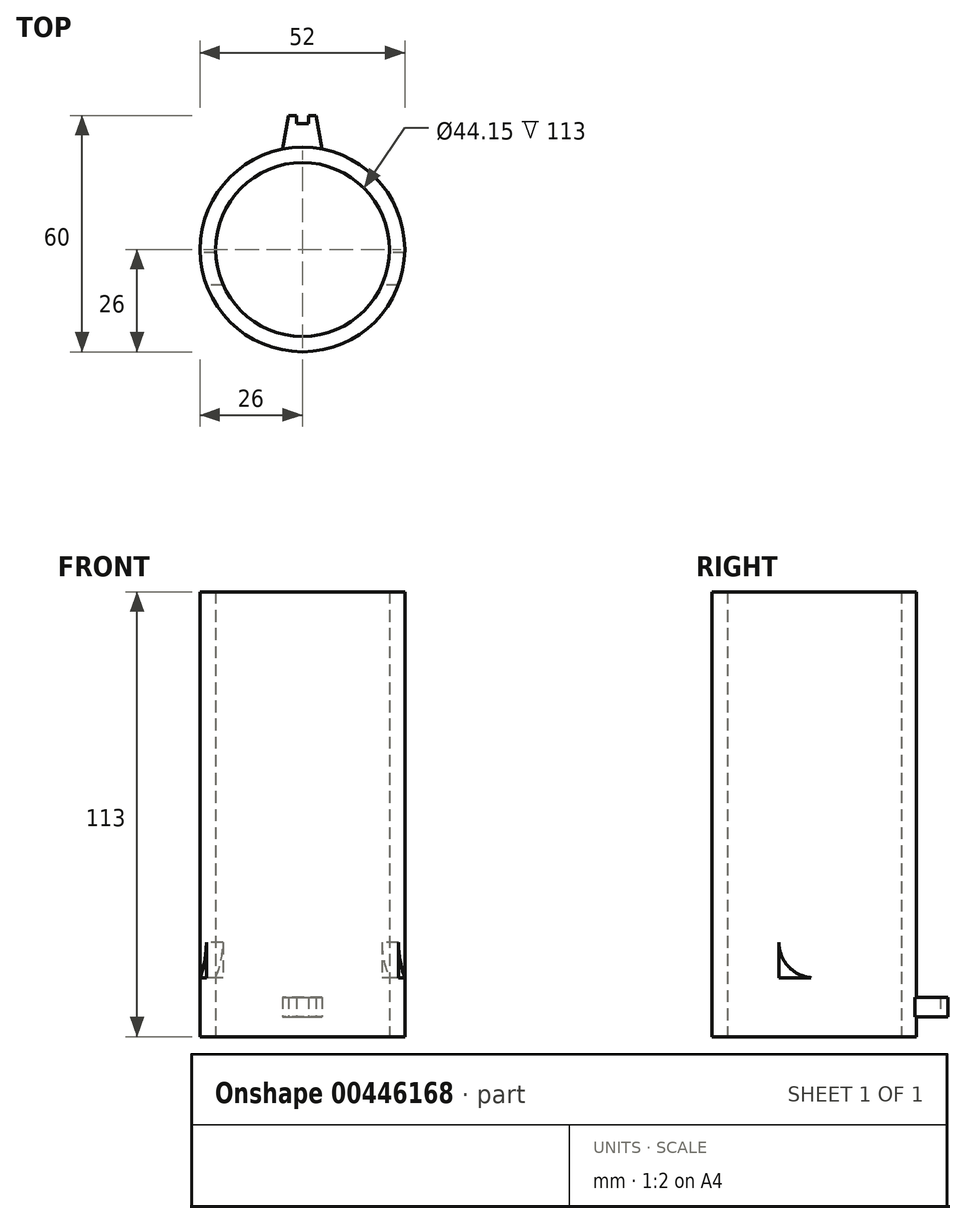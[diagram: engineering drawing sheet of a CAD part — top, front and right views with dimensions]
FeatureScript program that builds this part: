
annotation { "Feature Type Name" : "Feature", "Feature Type Description" : "" }
export const myFeature = defineFeature(function(context is Context, id is Id, definition is map)
    precondition{}
    {
        {
            var Q0;
            Q0=qCreatedBy(makeId("Top.planeOp"),FACE);
            var sketch = newSketch(context, id + "F0", { "sketchPlane" : qUnion([Q0])});
            skCircle(sketch, "E0", {"center": v(0, 0) * mm, "radius": 22.07 * mm});
            skCircle(sketch, "E1", {"center": v(0, 0) * mm, "radius": 26 * mm});
            skLineSegment(sketch, "E2", {"start": v(-5, 25.51) * mm, "end": v(-3.5, 34) * mm});
            skLineSegment(sketch, "E3", {"start": v(-3.5, 34) * mm, "end": v(-1.5, 34) * mm});
            skLineSegment(sketch, "E4", {"start": v(-1.5, 34) * mm, "end": v(-1.5, 32) * mm});
            skLineSegment(sketch, "E5", {"start": v(-1.5, 32) * mm, "end": v(1.5, 32) * mm});
            skLineSegment(sketch, "E6", {"start": v(1.5, 32) * mm, "end": v(1.5, 34) * mm});
            skPoint(sketch, "E7", {"position": v(5, 25.51) * mm});
            skLineSegment(sketch, "E8", {"start": v(1.5, 34) * mm, "end": v(3.5, 34) * mm});
            skLineSegment(sketch, "E9", {"start": v(3.5, 34) * mm, "end": v(5, 25.51) * mm});
            skSolve(sketch);
        }
        {
            var Q0;
            Q0=makeQuery(id+"F0.imprint","IMPRINT",FACE,{"disambiguationData":[TD([[makeQuery(id+"F0.imprint","IMPRINT",EDGE,{"derivedFrom":sQuery(id+"F0.wireOp",EDGE,"E0")}),-1.0]])]});
            extrude(context, id + "F1", {"entities" : qUnion([Q0]), "depth" : 113 * mm});
        }
        {
            var Q0;
            Q0=qCreatedBy(makeId("Right.planeOp"),FACE);
            var sketch = newSketch(context, id + "F2", { "sketchPlane" : qUnion([Q0])});
            skLineSegment(sketch, "E10.bottom", {"start": v(26, 113) * mm, "end": v(-26, 113) * mm});
            skLineSegment(sketch, "E10.top", {"start": v(26, 0) * mm, "end": v(-26, 0) * mm});
            skLineSegment(sketch, "E10.left", {"start": v(26, 113) * mm, "end": v(26, 0) * mm});
            skLineSegment(sketch, "E10.right", {"start": v(-26, 113) * mm, "end": v(-26, 0) * mm});
            skLineSegment(sketch, "E11", {"start": v(9, 15) * mm, "end": v(-9, 15) * mm});
            skLineSegment(sketch, "E12", {"start": v(-9, 15) * mm, "end": v(-9, 98) * mm});
            skLineSegment(sketch, "E13", {"start": v(-9, 98) * mm, "end": v(9, 98) * mm});
            skLineSegment(sketch, "E14", {"start": v(9, 98) * mm, "end": v(9, 15) * mm});
            skPoint(sketch, "E15", {"position": v(9, 89) * mm});
            skPoint(sketch, "E16", {"position": v(-9, 89) * mm});
            skArc(sketch, "E17", {"start": v(9, 89) * mm, "mid": v(0, 98.04) * mm, "end": v(-9, 89) * mm});
            skPoint(sketch, "E18", {"position": v(9, 24) * mm});
            skPoint(sketch, "E19", {"position": v(-9, 24) * mm});
            skArc(sketch, "E20", {"start": v(-9, 24) * mm, "mid": v(0, 14.96) * mm, "end": v(9, 24) * mm});
            skSolve(sketch);
        }
        {
            var Q0;
            {var subQ0=sQuery(id+"F2.wireOp",EDGE,"E20");var subQ12=sQuery(id+"F2.wireOp",EDGE,"E11");var subQ13=makeQuery(id+"F2.imprint","INTERSECT",VERTEX,{"disambiguationData":[OD(0.0)],"derivedFrom":[subQ12,subQ0]});Q0=makeQuery(id+"F2.imprint","IMPRINT",FACE,{"disambiguationData":[TD([[makeQuery(id+"F2.imprint","IMPRINT",EDGE,{"disambiguationData":[TD([[subQ13,-1.0]])],"derivedFrom":subQ12}),-1.0]])]});}
            extrude(context, id + "F3", {"entities" : qUnion([Q0]), "operationType" : NewBodyOperationType.REMOVE, "endBound" : BoundingType.SYMMETRIC, "depth" : 100 * mm});
        }
        {
            var Q0;
            {var subQ0=sQuery(id+"F0.wireOp",EDGE,"E2");Q0=makeQuery(id+"F0.imprint","IMPRINT",FACE,{"disambiguationData":[TD([[makeQuery(id+"F0.imprint","IMPRINT",EDGE,{"derivedFrom":subQ0}),-1.0]])]});}
            extrude(context, id + "F4", {"entities" : qUnion([Q0]), "operationType" : NewBodyOperationType.ADD, "depth" : 10 * mm});
        }
        {
            var Q0;
            {var subQ0=sQuery(id+"F0.wireOp",EDGE,"E2");Q0=makeQuery(id+"F0.imprint","IMPRINT",FACE,{"disambiguationData":[TD([[makeQuery(id+"F0.imprint","IMPRINT",EDGE,{"derivedFrom":subQ0}),-1.0]])]});}
            extrude(context, id + "F5", {"entities" : qUnion([Q0]), "operationType" : NewBodyOperationType.REMOVE, "depth" : 5 * mm});
        }
    });
